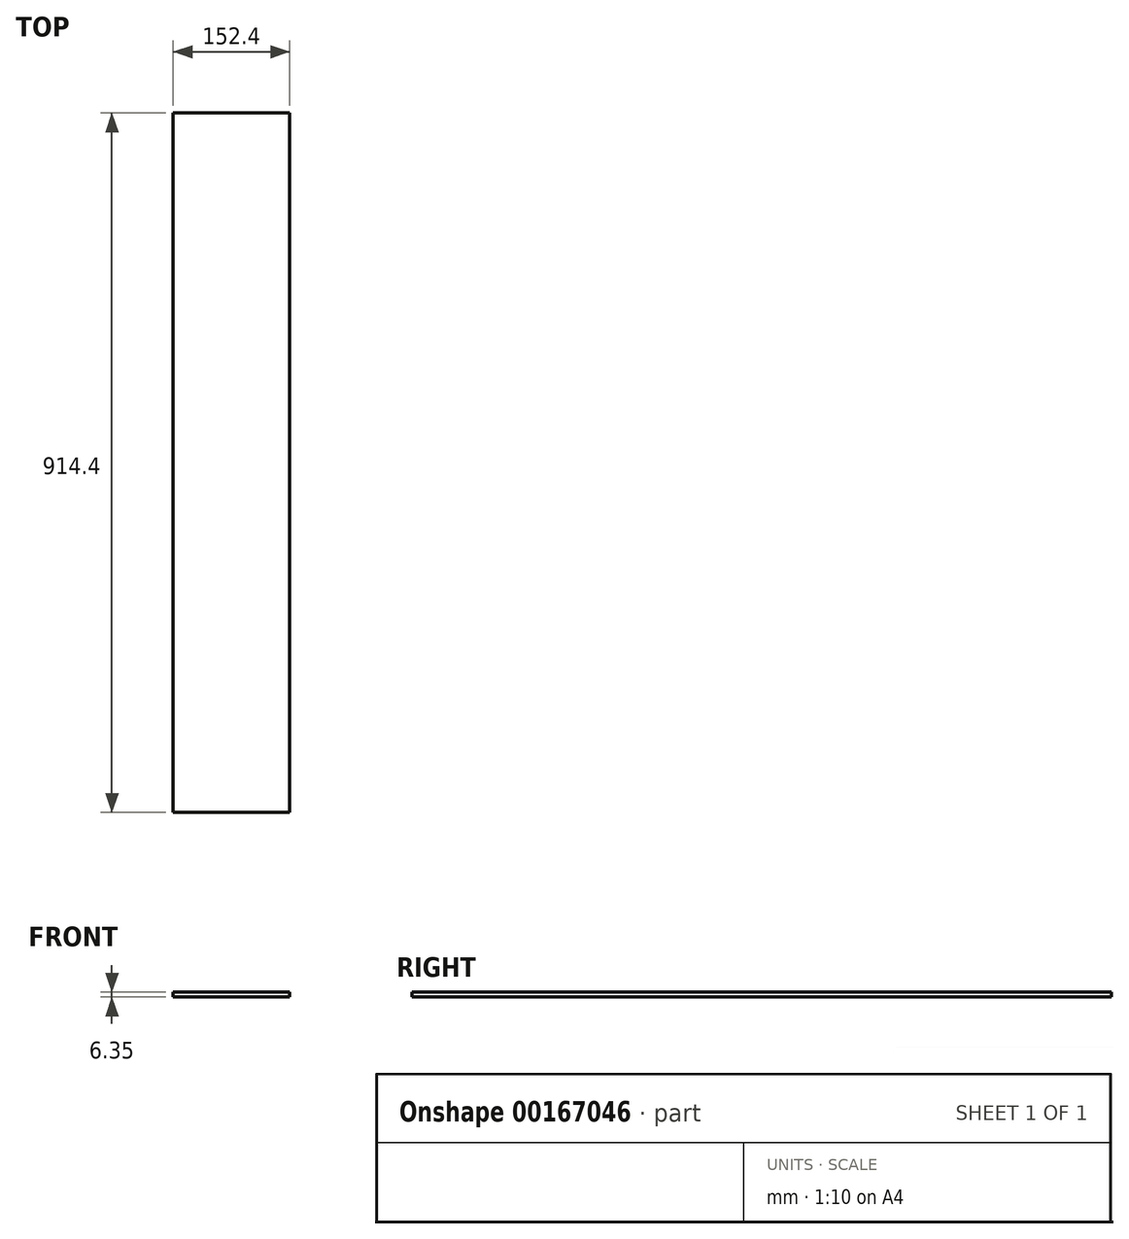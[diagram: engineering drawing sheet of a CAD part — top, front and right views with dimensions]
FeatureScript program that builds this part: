
annotation { "Feature Type Name" : "Feature", "Feature Type Description" : "" }
export const myFeature = defineFeature(function(context is Context, id is Id, definition is map)
    precondition{}
    {
        {
            var Q0;
            Q0=qCreatedBy(makeId("Top.planeOp"),FACE);
            var sketch = newSketch(context, id + "F0", { "sketchPlane" : qUnion([Q0])});
            skLineSegment(sketch, "E0.bottom", {"start": v(0, 0) * mm, "end": v(-152.4, 0) * mm});
            skLineSegment(sketch, "E0.top", {"start": v(0, 914.4) * mm, "end": v(-152.4, 914.4) * mm});
            skLineSegment(sketch, "E0.left", {"start": v(0, 0) * mm, "end": v(0, 914.4) * mm});
            skLineSegment(sketch, "E0.right", {"start": v(-152.4, 0) * mm, "end": v(-152.4, 914.4) * mm});
            skSolve(sketch);
        }
        {
            var Q0;
            Q0 = qSketchRegion(id + "F0", true);
            extrude(context, id + "F1", {"entities" : qUnion([Q0]), "depth" : 6.35 * mm});
        }
    });
